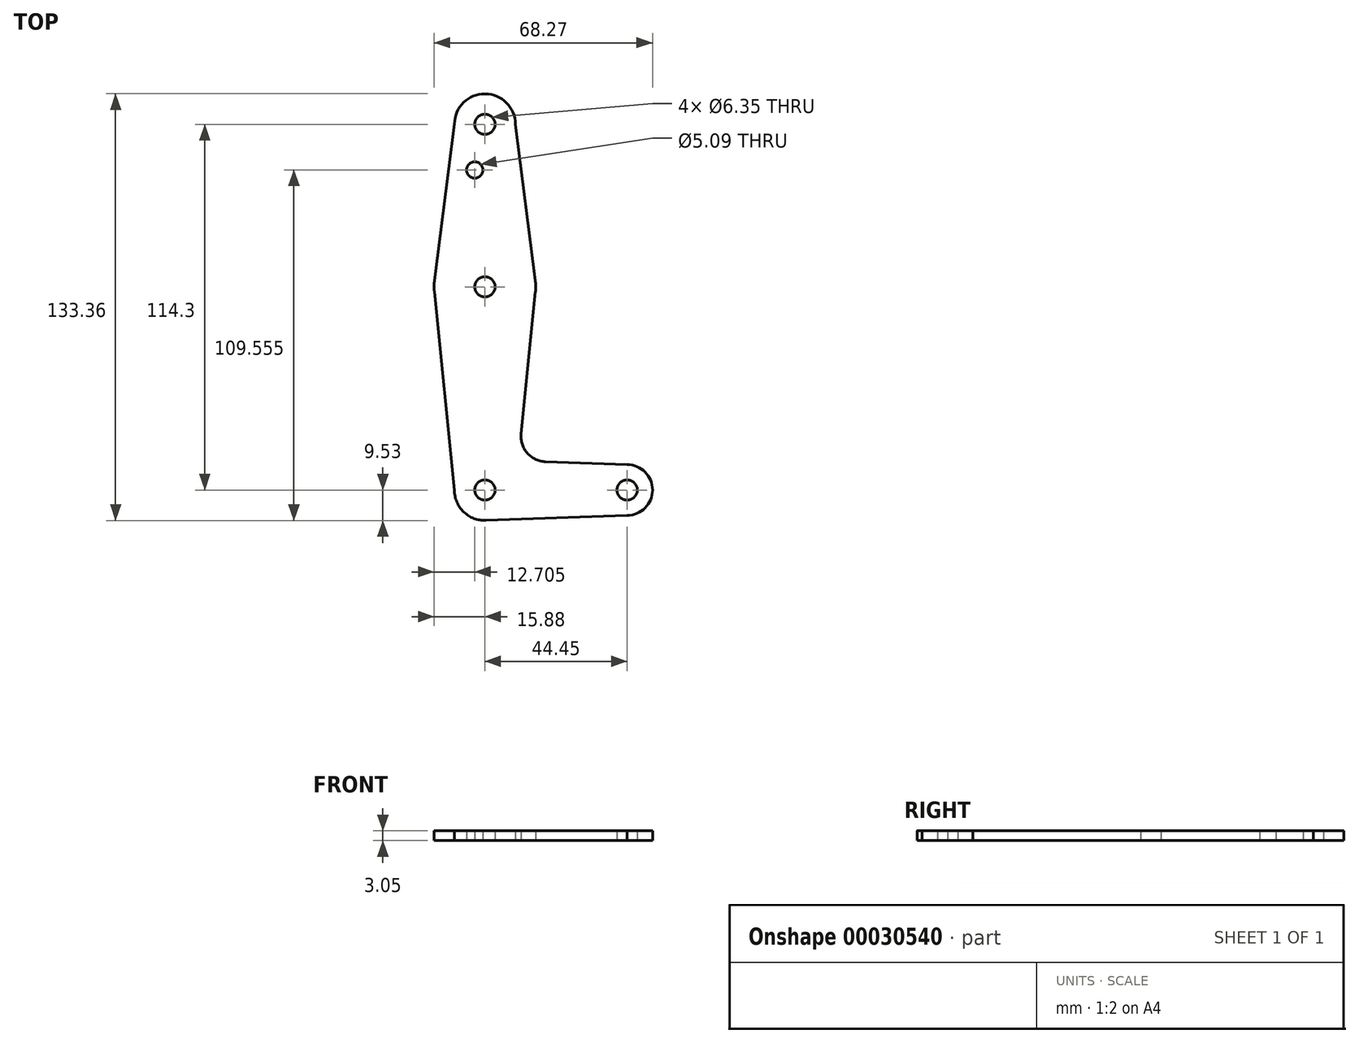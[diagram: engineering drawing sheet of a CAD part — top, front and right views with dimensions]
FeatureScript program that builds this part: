
annotation { "Feature Type Name" : "Feature", "Feature Type Description" : "" }
export const myFeature = defineFeature(function(context is Context, id is Id, definition is map)
    precondition{}
    {
        {
            var Q0;
            Q0=qCreatedBy(makeId("Top.planeOp"),FACE);
            var sketch = newSketch(context, id + "F0", { "sketchPlane" : qUnion([Q0])});
            skCircle(sketch, "E0", {"center": v(0, 0) * mm, "radius": 9.53 * mm});
            skCircle(sketch, "E1", {"center": v(0, 63.5) * mm, "radius": 15.88 * mm});
            skCircle(sketch, "E2", {"center": v(0, 114.3) * mm, "radius": 9.53 * mm});
            skCircle(sketch, "E3", {"center": v(44.45, 0) * mm, "radius": 7.94 * mm});
            skLineSegment(sketch, "E4", {"start": v(0, 114.3) * mm, "end": v(0, 0) * mm, "construction": true});
            skLineSegment(sketch, "E5", {"start": v(44.45, 0) * mm, "end": v(0, 0) * mm, "construction": true});
            skLineSegment(sketch, "E6", {"start": v(-9.52, 114.4) * mm, "end": v(-15.75, 65.5) * mm});
            skLineSegment(sketch, "E7", {"start": v(9.53, 114.3) * mm, "end": v(15.75, 65.5) * mm});
            skLineSegment(sketch, "E8", {"start": v(-9.53, 0) * mm, "end": v(-15.8, 61.9) * mm});
            skLineSegment(sketch, "E9", {"start": v(11.3, 17.6) * mm, "end": v(15.8, 61.9) * mm});
            skLineSegment(sketch, "E10", {"start": v(44.45, 7.94) * mm, "end": v(18.93, 8.85) * mm});
            skLineSegment(sketch, "E11", {"start": v(44.45, -7.94) * mm, "end": v(0, -9.53) * mm});
            skCircle(sketch, "E12", {"center": v(0, 114.3) * mm, "radius": 3.18 * mm});
            skCircle(sketch, "E13", {"center": v(0, 63.5) * mm, "radius": 3.18 * mm});
            skCircle(sketch, "E14", {"center": v(0, 0) * mm, "radius": 3.18 * mm});
            skCircle(sketch, "E15", {"center": v(44.45, 0) * mm, "radius": 3.18 * mm});
            skCircle(sketch, "E16", {"center": v(-3.17, 100.03) * mm, "radius": 2.54 * mm});
            skPoint(sketch, "E17.newPointB", {"position": v(0, 9.53) * mm});
            skArc(sketch, "E17.filletArc", {"start": v(11.3, 17.6) * mm, "mid": v(13.22, 11.57) * mm, "end": v(18.93, 8.85) * mm});
            skSolve(sketch);
        }
        {
            var Q0;
            Q0 = qSketchRegion(id + "F0", true);
            extrude(context, id + "F1", {"entities" : qUnion([Q0]), "depth" : 3.05 * mm});
        }
    });
